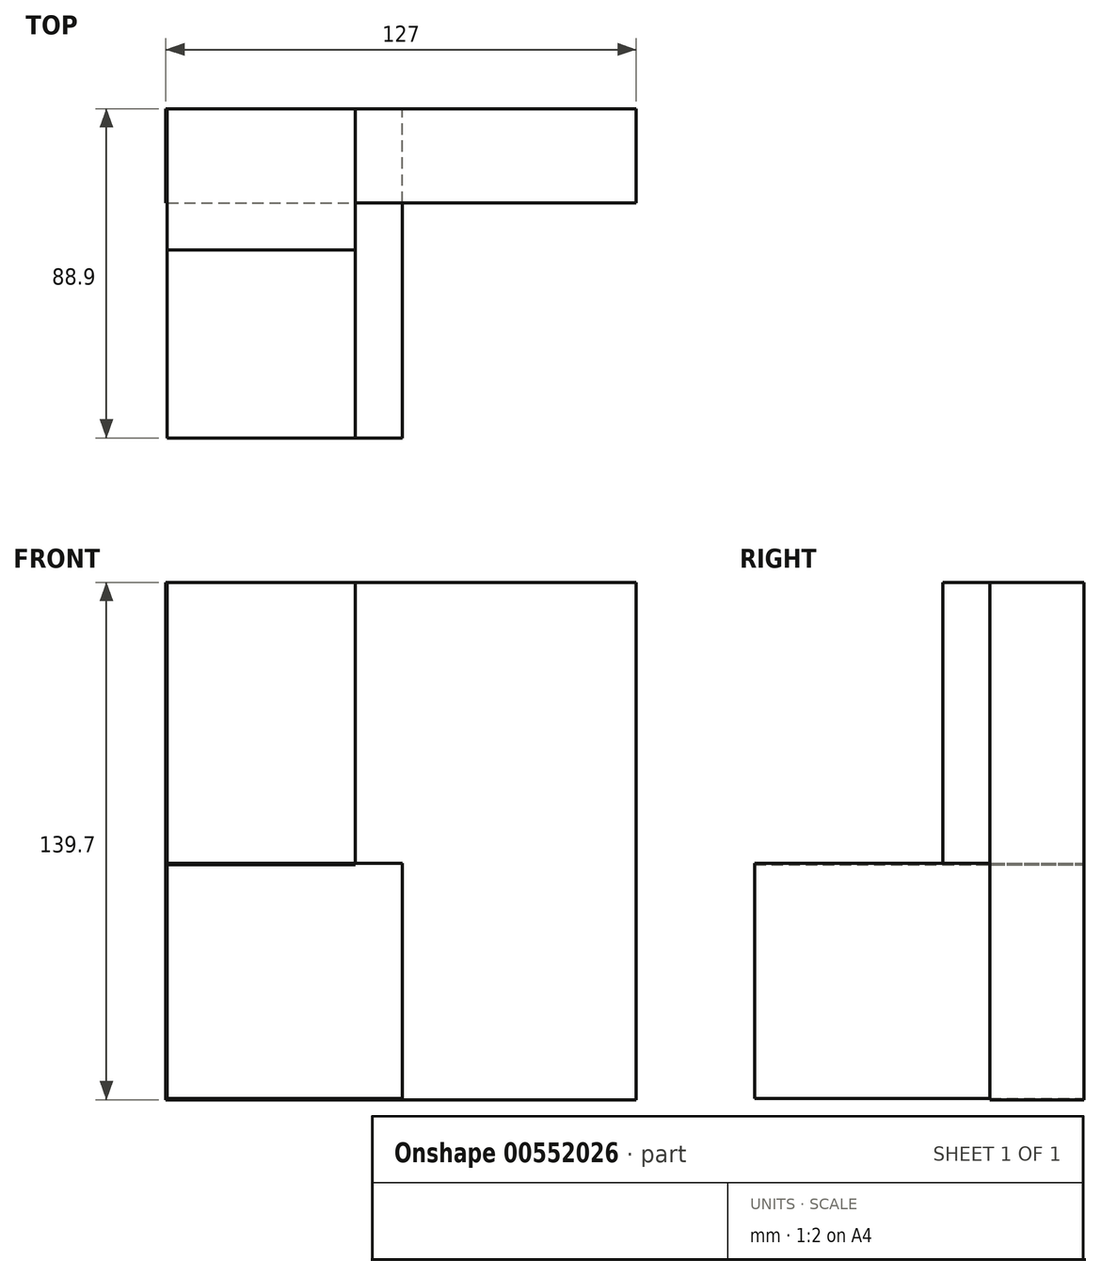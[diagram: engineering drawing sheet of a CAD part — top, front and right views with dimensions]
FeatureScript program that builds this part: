
annotation { "Feature Type Name" : "Feature", "Feature Type Description" : "" }
export const myFeature = defineFeature(function(context is Context, id is Id, definition is map)
    precondition{}
    {
        {
            var Q0;
            Q0=qCreatedBy(makeId("Front.planeOp"),FACE);
            var sketch = newSketch(context, id + "F0", { "sketchPlane" : qUnion([Q0])});
            skPoint(sketch, "E0.bottom.end.orphan", {"position": v(0, 94.7) * mm});
            skLineSegment(sketch, "E1.bottom", {"start": v(-61.88, -6.53) * mm, "end": v(1.62, -6.53) * mm});
            skLineSegment(sketch, "E1.top", {"start": v(-61.88, -70.03) * mm, "end": v(1.62, -70.03) * mm});
            skLineSegment(sketch, "E1.left", {"start": v(-61.88, -6.53) * mm, "end": v(-61.88, -70.03) * mm});
            skLineSegment(sketch, "E1.right", {"start": v(1.62, -6.53) * mm, "end": v(1.62, -70.03) * mm});
            skLineSegment(sketch, "E2.bottom", {"start": v(-61.94, 69.32) * mm, "end": v(-11.14, 69.32) * mm});
            skLineSegment(sketch, "E2.top", {"start": v(-61.94, -6.88) * mm, "end": v(-11.14, -6.88) * mm});
            skLineSegment(sketch, "E2.left", {"start": v(-61.94, 69.32) * mm, "end": v(-61.94, -6.88) * mm});
            skLineSegment(sketch, "E2.right", {"start": v(-11.14, 69.32) * mm, "end": v(-11.14, -6.88) * mm});
            skLineSegment(sketch, "E3.bottom", {"start": v(-62.28, 69.32) * mm, "end": v(64.72, 69.32) * mm});
            skLineSegment(sketch, "E3.top", {"start": v(-62.28, -70.38) * mm, "end": v(64.72, -70.38) * mm});
            skLineSegment(sketch, "E3.left", {"start": v(-62.28, 69.32) * mm, "end": v(-62.28, -70.38) * mm});
            skLineSegment(sketch, "E3.right", {"start": v(64.72, 69.32) * mm, "end": v(64.72, -70.38) * mm});
            skSolve(sketch);
        }
        {
            var Q0;
            {var subQ2=sQuery(id+"F0.wireOp",EDGE,"E1.top");Q0=makeQuery(id+"F0.imprint","IMPRINT",FACE,{"disambiguationData":[TD([[makeQuery(id+"F0.imprint","IMPRINT",EDGE,{"derivedFrom":subQ2}),1.0]])]});}
            extrude(context, id + "F1", {"entities" : qUnion([Q0]), "depth" : 88.9 * mm, "offsetDistance" : 25.4 * mm});
        }
        {
            var Q0;
            {var subQ0=sQuery(id+"F0.wireOp",EDGE,"E2.left");Q0=makeQuery(id+"F0.imprint","IMPRINT",FACE,{"disambiguationData":[TD([[makeQuery(id+"F0.imprint","IMPRINT",EDGE,{"derivedFrom":subQ0}),1.0]])]});}
            extrude(context, id + "F2", {"entities" : qUnion([Q0]), "depth" : 38.1 * mm, "offsetDistance" : 25.4 * mm});
        }
        {
            var Q0;
            {var subQ12=sQuery(id+"F0.wireOp",EDGE,"E1.top");Q0=makeQuery(id+"F0.imprint","IMPRINT",FACE,{"disambiguationData":[TD([[makeQuery(id+"F0.imprint","IMPRINT",EDGE,{"derivedFrom":subQ12}),-1.0]])]});}
            extrude(context, id + "F3", {"entities" : qUnion([Q0]), "depth" : 25.4 * mm, "offsetDistance" : 25.4 * mm});
        }
    });
